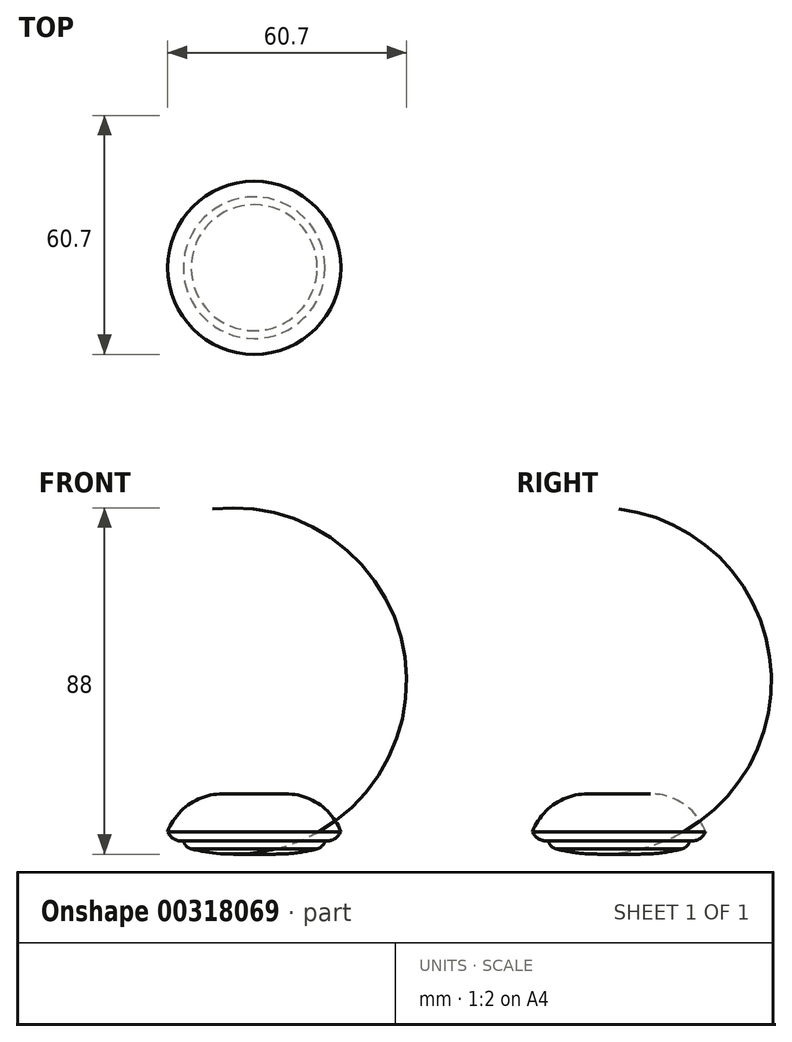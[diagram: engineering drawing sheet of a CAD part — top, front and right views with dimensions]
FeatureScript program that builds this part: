
annotation { "Feature Type Name" : "Feature", "Feature Type Description" : "" }
export const myFeature = defineFeature(function(context is Context, id is Id, definition is map)
    precondition{}
    {
        {
            var Q0;
            Q0=qCreatedBy(makeId("Front.planeOp"),FACE);
            var sketch = newSketch(context, id + "F0", { "sketchPlane" : qUnion([Q0])});
            skLineSegment(sketch, "E0", {"start": v(0, 0) * mm, "end": v(8, 0) * mm});
            skArc(sketch, "E1", {"start": v(22, -9.61) * mm, "mid": v(16.5, -2.64) * mm, "end": v(8, 0) * mm});
            skArc(sketch, "E2", {"start": v(18, -12) * mm, "mid": v(20.38, -11.45) * mm, "end": v(22, -9.61) * mm});
            skLineSegment(sketch, "E3", {"start": v(18, -12) * mm, "end": v(0, -12) * mm});
            skArc(sketch, "E4", {"start": v(16, -14) * mm, "mid": v(17.25, -13.25) * mm, "end": v(18, -12) * mm});
            skArc(sketch, "E5", {"start": v(0, -15) * mm, "mid": v(8.05, -15.23) * mm, "end": v(16, -14) * mm});
            skLineSegment(sketch, "E6", {"start": v(16, -14) * mm, "end": v(0, -14) * mm});
            skLineSegment(sketch, "E7", {"start": v(0, -14) * mm, "end": v(0, -15) * mm});
            skLineSegment(sketch, "E8", {"start": v(0, -14) * mm, "end": v(0, -12) * mm});
            skLineSegment(sketch, "E9", {"start": v(0, -12) * mm, "end": v(0, 0) * mm});
            skSolve(sketch);
        }
        {
            var Q0;
            Q0=makeQuery(id+"F0.imprint","IMPRINT",FACE,{"disambiguationData":[TD([[makeQuery(id+"F0.imprint","IMPRINT",EDGE,{"derivedFrom":sQuery(id+"F0.wireOp",EDGE,"E5")}),1.0]])]});
            var Q1;
            Q1=makeQuery(id+"F0.imprint","IMPRINT",FACE,{"disambiguationData":[TD([[makeQuery(id+"F0.imprint","IMPRINT",EDGE,{"derivedFrom":sQuery(id+"F0.wireOp",EDGE,"E3")}),1.0]])]});
            var Q2;
            Q2=makeQuery(id+"F0.imprint","IMPRINT",FACE,{"disambiguationData":[TD([[makeQuery(id+"F0.imprint","IMPRINT",EDGE,{"derivedFrom":sQuery(id+"F0.wireOp",EDGE,"E0")}),-1.0]])]});
            var Q3;
            Q3=sQuery(id+"F0.wireOp",EDGE,"E9");
            revolve(context, id + "F1", {"entities" : qUnion([Q0, Q1, Q2]), "axis" : qUnion([Q3]), "revolveType" : RevolveType.FULL});
        }
    });
